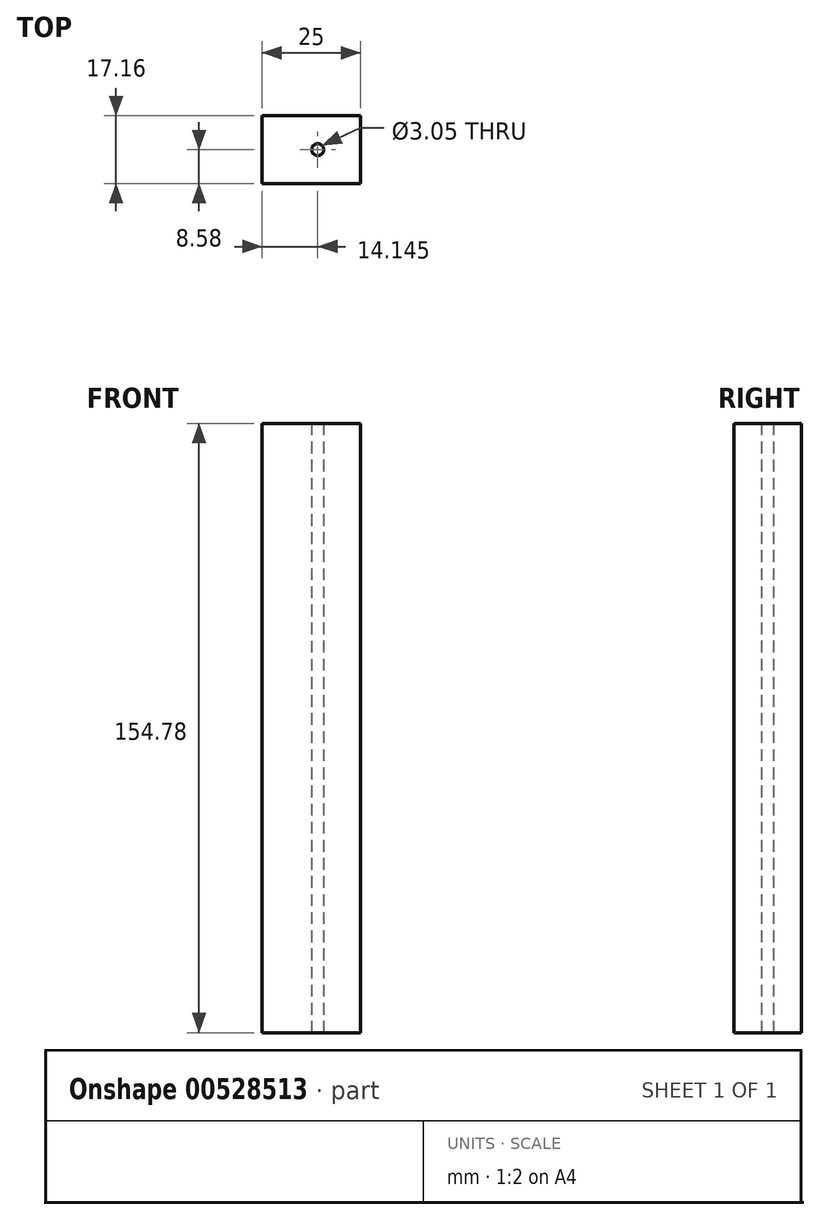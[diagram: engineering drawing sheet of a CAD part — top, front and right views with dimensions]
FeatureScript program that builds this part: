
annotation { "Feature Type Name" : "Feature", "Feature Type Description" : "" }
export const myFeature = defineFeature(function(context is Context, id is Id, definition is map)
    precondition{}
    {
        {
            var Q0;
            Q0=qCreatedBy(makeId("Right.planeOp"),FACE);
            var sketch = newSketch(context, id + "F0", { "sketchPlane" : qUnion([Q0])});
            skLineSegment(sketch, "E0.bottom", {"start": v(0, 23.9) * mm, "end": v(0, 23.9) * mm});
            skLineSegment(sketch, "E0.top", {"start": v(0, 14.09) * mm, "end": v(0, 14.09) * mm});
            skLineSegment(sketch, "E0.left", {"start": v(0, 23.9) * mm, "end": v(0, 14.09) * mm});
            skLineSegment(sketch, "E0.right", {"start": v(0, 23.9) * mm, "end": v(0, 14.09) * mm});
            skPoint(sketch, "E0.middle", {"position": v(0, 18.99) * mm});
            skLineSegment(sketch, "E1.bottom", {"start": v(8.58, 54.11) * mm, "end": v(-8.58, 54.11) * mm});
            skLineSegment(sketch, "E1.top", {"start": v(8.58, -100.67) * mm, "end": v(-8.58, -100.67) * mm});
            skLineSegment(sketch, "E1.left", {"start": v(8.58, 54.11) * mm, "end": v(8.58, -100.67) * mm});
            skLineSegment(sketch, "E1.right", {"start": v(-8.58, 54.11) * mm, "end": v(-8.58, -100.67) * mm});
            skPoint(sketch, "E1.middle", {"position": v(0, -23.28) * mm});
            skSolve(sketch);
        }
        {
            var Q0;
            Q0=makeQuery(id+"F0.imprint","IMPRINT",FACE,{"disambiguationData":[TD([[makeQuery(id+"F0.imprint","IMPRINT",EDGE,{"derivedFrom":sQuery(id+"F0.wireOp",EDGE,"E1.bottom")}),1.0]])]});
            extrude(context, id + "F1", {"entities" : qUnion([Q0]), "depth" : 25 * mm, "offsetDistance" : 25 * mm});
        }
        {
            var Q0;
            Q0=makeQuery(id+"F1.opExtrude","SWEPT_FACE",FACE,{"disambiguationData":[OSD([sQuery(id+"F0.wireOp",EDGE,"E1.top")])]});
            var sketch = newSketch(context, id + "F2", { "sketchPlane" : qUnion([Q0])});
            skCircle(sketch, "E2", {"center": v(14.14, 0) * mm, "radius": 6.63 * mm});
            skSolve(sketch);
        }
        {
            var Q0;
            Q0=sQuery(id+"F2.wireOp",VERTEX,"E2.center");
            var Q1;
            Q1=makeQuery(id+"F1.opExtrude","SWEPT_BODY",BODY,{"disambiguationData":[OSD([sQuery(id+"F0.wireOp",EDGE,"E1.bottom"),sQuery(id+"F0.wireOp",EDGE,"E1.top"),sQuery(id+"F0.wireOp",EDGE,"E1.left"),sQuery(id+"F0.wireOp",EDGE,"E1.right")])]});
            hole(context, id + "F3", {"style" : HoleStyle.SIMPLE, "endStyle" : HoleEndStyle.THROUGH, "holeDiameter" : 3.05 * mm, "isTappedThrough" : true, "tappedDepth" : 12 * mm, "tapClearance" : 3, "locations" : qUnion([Q0]), "scope" : qUnion([Q1])});
        }
    });
